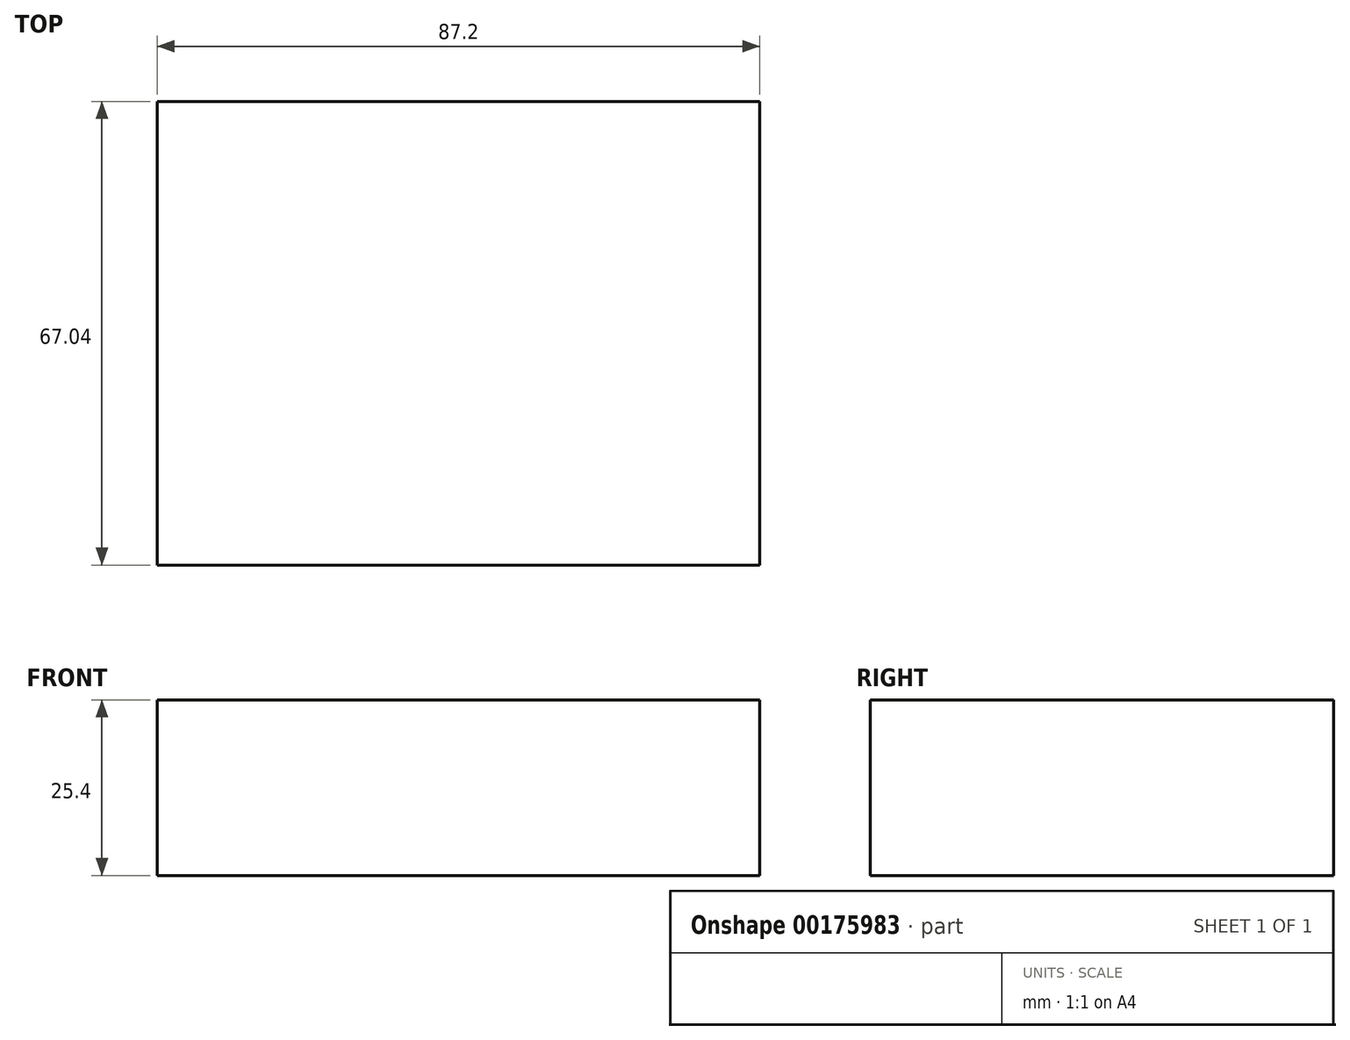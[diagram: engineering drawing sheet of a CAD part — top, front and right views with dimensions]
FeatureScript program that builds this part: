
annotation { "Feature Type Name" : "Feature", "Feature Type Description" : "" }
export const myFeature = defineFeature(function(context is Context, id is Id, definition is map)
    precondition{}
    {
        {
            var Q0;
            Q0=qCreatedBy(makeId("Top.planeOp"),FACE);
            var sketch = newSketch(context, id + "F0", { "sketchPlane" : qUnion([Q0])});
            skLineSegment(sketch, "E0.bottom", {"start": v(43.6, 33.52) * mm, "end": v(-43.6, 33.52) * mm});
            skLineSegment(sketch, "E0.top", {"start": v(43.6, -33.52) * mm, "end": v(-43.6, -33.52) * mm});
            skLineSegment(sketch, "E0.left", {"start": v(43.6, 33.52) * mm, "end": v(43.6, -33.52) * mm});
            skLineSegment(sketch, "E0.right", {"start": v(-43.6, 33.52) * mm, "end": v(-43.6, -33.52) * mm});
            skPoint(sketch, "E0.middle", {"position": v(0, 0) * mm});
            skCircle(sketch, "E1", {"center": v(0, 0) * mm, "radius": 55 * mm});
            skSolve(sketch);
        }
        {
            var Q0;
            Q0=makeQuery(id+"F0.imprint","IMPRINT",FACE,{"disambiguationData":[TD([[makeQuery(id+"F0.imprint","IMPRINT",EDGE,{"derivedFrom":sQuery(id+"F0.wireOp",EDGE,"E0.bottom")}),1.0]])]});
            extrude(context, id + "F1", {"entities" : qUnion([Q0]), "depth" : 25.4 * mm});
        }
    });
